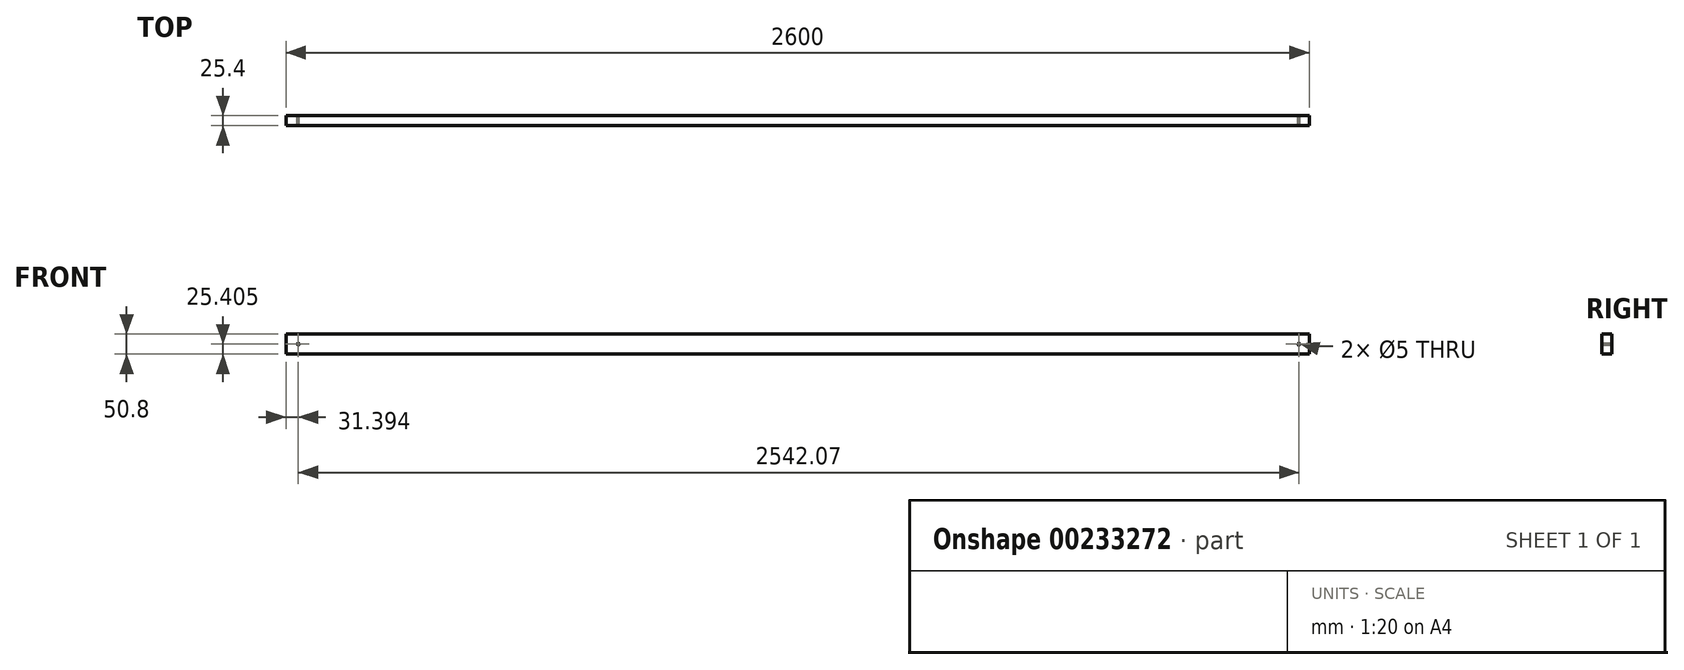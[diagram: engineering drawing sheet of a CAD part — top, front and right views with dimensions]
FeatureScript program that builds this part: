
annotation { "Feature Type Name" : "Feature", "Feature Type Description" : "" }
export const myFeature = defineFeature(function(context is Context, id is Id, definition is map)
    precondition{}
    {
        {
            var Q0;
            Q0=qCreatedBy(makeId("Front.planeOp"),FACE);
            var sketch = newSketch(context, id + "F0", { "sketchPlane" : qUnion([Q0])});
            skLineSegment(sketch, "E0.bottom", {"start": v(-1301.93, -312.24) * mm, "end": v(1298.07, -312.24) * mm});
            skLineSegment(sketch, "E0.top", {"start": v(-1301.93, -363.04) * mm, "end": v(1298.07, -363.04) * mm});
            skLineSegment(sketch, "E0.left", {"start": v(-1301.93, -312.24) * mm, "end": v(-1301.93, -363.04) * mm});
            skLineSegment(sketch, "E0.right", {"start": v(1298.07, -312.24) * mm, "end": v(1298.07, -363.04) * mm});
            skCircle(sketch, "E1", {"center": v(1271.53, -337.64) * mm, "radius": 2.5 * mm});
            skCircle(sketch, "E2", {"center": v(-1270.54, -337.64) * mm, "radius": 2.5 * mm});
            skSolve(sketch);
        }
        {
            var Q0;
            Q0 = qSketchRegion(id + "F0", true);
            extrude(context, id + "F1", {"entities" : qUnion([Q0]), "depth" : 25.4 * mm});
        }
    });
